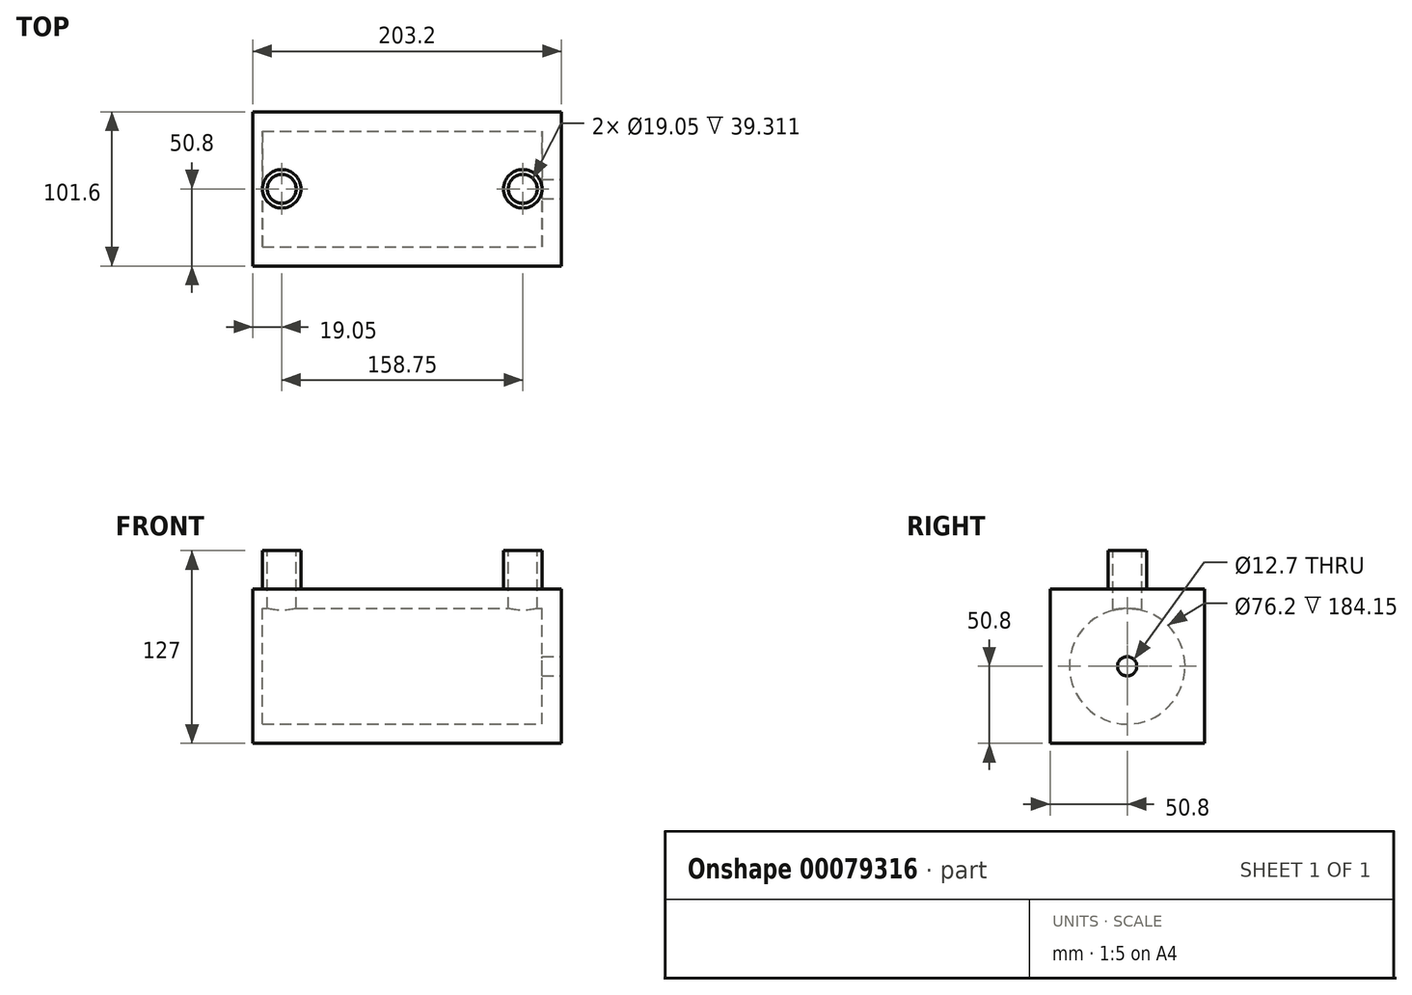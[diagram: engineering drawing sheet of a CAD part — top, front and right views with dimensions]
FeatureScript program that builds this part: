
annotation { "Feature Type Name" : "Feature", "Feature Type Description" : "" }
export const myFeature = defineFeature(function(context is Context, id is Id, definition is map)
    precondition{}
    {
        {
            var Q0;
            Q0=qCreatedBy(makeId("Right.planeOp"),FACE);
            var sketch = newSketch(context, id + "F0", { "sketchPlane" : qUnion([Q0])});
            skLineSegment(sketch, "E0.bottom", {"start": v(-50.8, 50.8) * mm, "end": v(50.8, 50.8) * mm});
            skLineSegment(sketch, "E0.top", {"start": v(-50.8, -50.8) * mm, "end": v(50.8, -50.8) * mm});
            skLineSegment(sketch, "E0.left", {"start": v(-50.8, 50.8) * mm, "end": v(-50.8, -50.8) * mm});
            skLineSegment(sketch, "E0.right", {"start": v(50.8, 50.8) * mm, "end": v(50.8, -50.8) * mm});
            skPoint(sketch, "E0.middle", {"position": v(0, 0) * mm});
            skSolve(sketch);
        }
        {
            var Q0;
            Q0 = qSketchRegion(id + "F0", true);
            extrude(context, id + "F1", {"entities" : qUnion([Q0]), "endBound" : BoundingType.SYMMETRIC, "depth" : 203.2 * mm});
        }
        {
            var Q0;
            Q0=makeQuery(id+"F1.opExtrude","CAP_FACE",FACE,{"disambiguationData":[OSD([sQuery(id+"F0.wireOp",EDGE,"E0.bottom"),sQuery(id+"F0.wireOp",EDGE,"E0.top"),sQuery(id+"F0.wireOp",EDGE,"E0.left"),sQuery(id+"F0.wireOp",EDGE,"E0.right")])],"isStart":false});
            cPlane(context, id + "F2", {"entities" : qUnion([Q0]), "cplaneType" : CPlaneType.OFFSET, "offset" : 12.7 * mm, "oppositeDirection" : true, "width" : 152.4 * mm, "height" : 152.4 * mm});
        }
        {
            var Q0;
            Q0=qCreatedBy(id+"F2.planeOp",FACE);
            var sketch = newSketch(context, id + "F3", { "sketchPlane" : qUnion([Q0])});
            skCircle(sketch, "E1", {"center": v(0, 0) * mm, "radius": 38.1 * mm});
            skSolve(sketch);
        }
        {
            var Q0;
            Q0 = qSketchRegion(id + "F3", true);
            extrude(context, id + "F4", {"entities" : qUnion([Q0]), "operationType" : NewBodyOperationType.REMOVE, "oppositeDirection" : true, "depth" : 184.15 * mm});
        }
        {
            var Q0;
            Q0=makeQuery(id+"F1.opExtrude","CAP_FACE",FACE,{"disambiguationData":[OSD([sQuery(id+"F0.wireOp",EDGE,"E0.bottom"),sQuery(id+"F0.wireOp",EDGE,"E0.top"),sQuery(id+"F0.wireOp",EDGE,"E0.left"),sQuery(id+"F0.wireOp",EDGE,"E0.right")])],"isStart":false});
            var sketch = newSketch(context, id + "F5", { "sketchPlane" : qUnion([Q0])});
            skCircle(sketch, "E2", {"center": v(0, 0) * mm, "radius": 6.35 * mm});
            skSolve(sketch);
        }
        {
            var Q0;
            Q0 = qSketchRegion(id + "F5", true);
            extrude(context, id + "F6", {"entities" : qUnion([Q0]), "operationType" : NewBodyOperationType.REMOVE, "endBound" : BoundingType.UP_TO_NEXT, "oppositeDirection" : true, "depth" : 25.4 * mm});
        }
        {
            var Q0;
            Q0=makeQuery(id+"F1.opExtrude","SWEPT_FACE",FACE,{"disambiguationData":[OSD([sQuery(id+"F0.wireOp",EDGE,"E0.bottom")])]});
            var sketch = newSketch(context, id + "F7", { "sketchPlane" : qUnion([Q0])});
            skCircle(sketch, "E3", {"center": v(-82.55, 0) * mm, "radius": 9.53 * mm});
            skCircle(sketch, "E4", {"center": v(76.2, 0) * mm, "radius": 9.53 * mm});
            skSolve(sketch);
        }
        {
            var Q0;
            Q0 = qSketchRegion(id + "F7", true);
            extrude(context, id + "F8", {"entities" : qUnion([Q0]), "operationType" : NewBodyOperationType.REMOVE, "oppositeDirection" : true, "depth" : 25.4 * mm});
        }
        {
            var Q0;
            Q0=makeQuery(id+"F1.opExtrude","SWEPT_FACE",FACE,{"disambiguationData":[OSD([sQuery(id+"F0.wireOp",EDGE,"E0.bottom")])]});
            var sketch = newSketch(context, id + "F9", { "sketchPlane" : qUnion([Q0])});
            skCircle(sketch, "E5", {"center": v(-82.55, 0) * mm, "radius": 12.7 * mm});
            skCircle(sketch, "E6", {"center": v(76.2, 0) * mm, "radius": 12.7 * mm});
            skCircle(sketch, "E7", {"center": v(76.2, 0) * mm, "radius": 9.53 * mm});
            skCircle(sketch, "E8", {"center": v(-82.55, 0) * mm, "radius": 9.53 * mm});
            skSolve(sketch);
        }
        {
            var Q0;
            Q0 = qSketchRegion(id + "F9", true);
            extrude(context, id + "F10", {"entities" : qUnion([Q0]), "operationType" : NewBodyOperationType.ADD, "depth" : 25.4 * mm});
        }
    });
